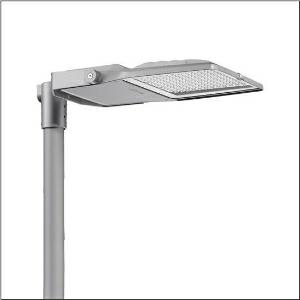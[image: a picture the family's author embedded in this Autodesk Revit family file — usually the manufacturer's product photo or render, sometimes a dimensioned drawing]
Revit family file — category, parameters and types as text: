
# Revit family: floodlight_fl_21_iq_midi___pl52_5xa7781e4d3a_f0c1
name_source: partatom
category: Lighting Fixtures
units: mm (PartAtom-declared; Revit-internal decimal feet)

## family parameters
Cut with Voids When Loaded = No
Host = Face
Light Source = No
Part Type = Normal
Room Calculation Point = No
Round Connector Dimension = Use Diameter
Shared = No

## types (1)
- --- (1 x LED, 28010 lm, 208.1 W, 4000K)
    Apparent Load = 208 VA
    CIE Flux Codes = 26 60 98 100 100
    Color Rendering = 70
    Color Temperature = 4000K
    Default Elevation = 1800 mm
    Description = Floodlight FL 21 iQ midi, floodlight, primary light control with lens, of PMMA, primary optical cover: protective disc, of toughened safety glass, transparent, light distribution: PL52, light emission: direct distribution, installation type: surface-mounted, LED, High Power LED, rated luminous flux: 28.010lm, luminous efficacy: 135lm/W, light colour: 740, colour temperature: 4000K, control gear: iQ Comfort/DALI, control: optimised constant luminous flux control (CLO 2.0), Desk-Remote (wireless, voltage-free reading and setting of iQ features in the workshop via application-optimized NFC function/RFID function), Light-Fading, Smart-Wire, Night-Set, Lumen-Switch, Temp-Guard, Auto-Match, with terminal, 6-pole, mains connection: 220..240V, AC, 50/60Hz, start of lifetime: 208W, end of service life: 227W, reduction: 90W, luminaire housing, of diecast aluminium, powder-coated, Siteco® metallic grey (DB 702S), corrosivity category C5 mid according to DIN EN ISO 12944, suitable for swimming pools, chlorine-resistant, sealing non-destructively replaceable, please order mast flange separately, mast bracket, of steel, galvanised, powder-coated, Siteco® metallic grey (DB 702S), protection rating (complete): IP66, insulation class (complete): insulation class II (safety insulation), certification: CE, ENEC, VDE, protection symbol: D, impact resistance: IK08, permissible operating ambient temperature: -40..+40°C, permissible operating ambient temperature for outdoor applications: -40..+50°C, standard: DIN EN 12944, LABS conformity tested according to VDMA 24364:2018-05, packaging unit: 1 piece

Light Distribution: PL52
    Height = 76 mm
    Lamp = 1 x LED
    Lamp Light Flux = 28010 lm
    Lamp Power = 208.1 W
    Lamp count = 1
    Length = 657 mm
    Luminous efficacy = 135 lm/W
    Manufacturer = Siteco
    ModVariant = No
    Model = 5XA7781E4D3A
    Number of Poles = 1
    OnlyDefault = Yes
    Power Factor = 1
    Product Name = Floodlight FL 21 iQ midi | PL52
    Product group = floodlight | pylon annexe
    ProductGroupID = 6200
    Protection Class = Protection class II
    Protection Degree = IP 66
    RLX_Detail_Level = 1
    RLX_Emergency_Light_Flux = 0 lm
    RLX_Emergency_Type = 0
    RLX_Emergency_Type_DB = No
    RlxData = <blob elided: 153857 chars, md5=0986a958>
    Socket = socket
    Standby Power = 0 W
    System Light Flux = 28010 lm
    System Power = 208 W
    Type Comments = factory setting: luminous flux: 100 % | dim-lin: 254 | 710 mA
    Type Image = l_1007123.jpg
    URL = http://relux.com
    VarID = @adj_106200
    Voltage = 0 V
    Weight = 0.00 kg
    Width = 442 mm

## geometry (parser evidence)
native form markers: Blend x4, Sweep x15
no freeform markers — native parametric forms only
